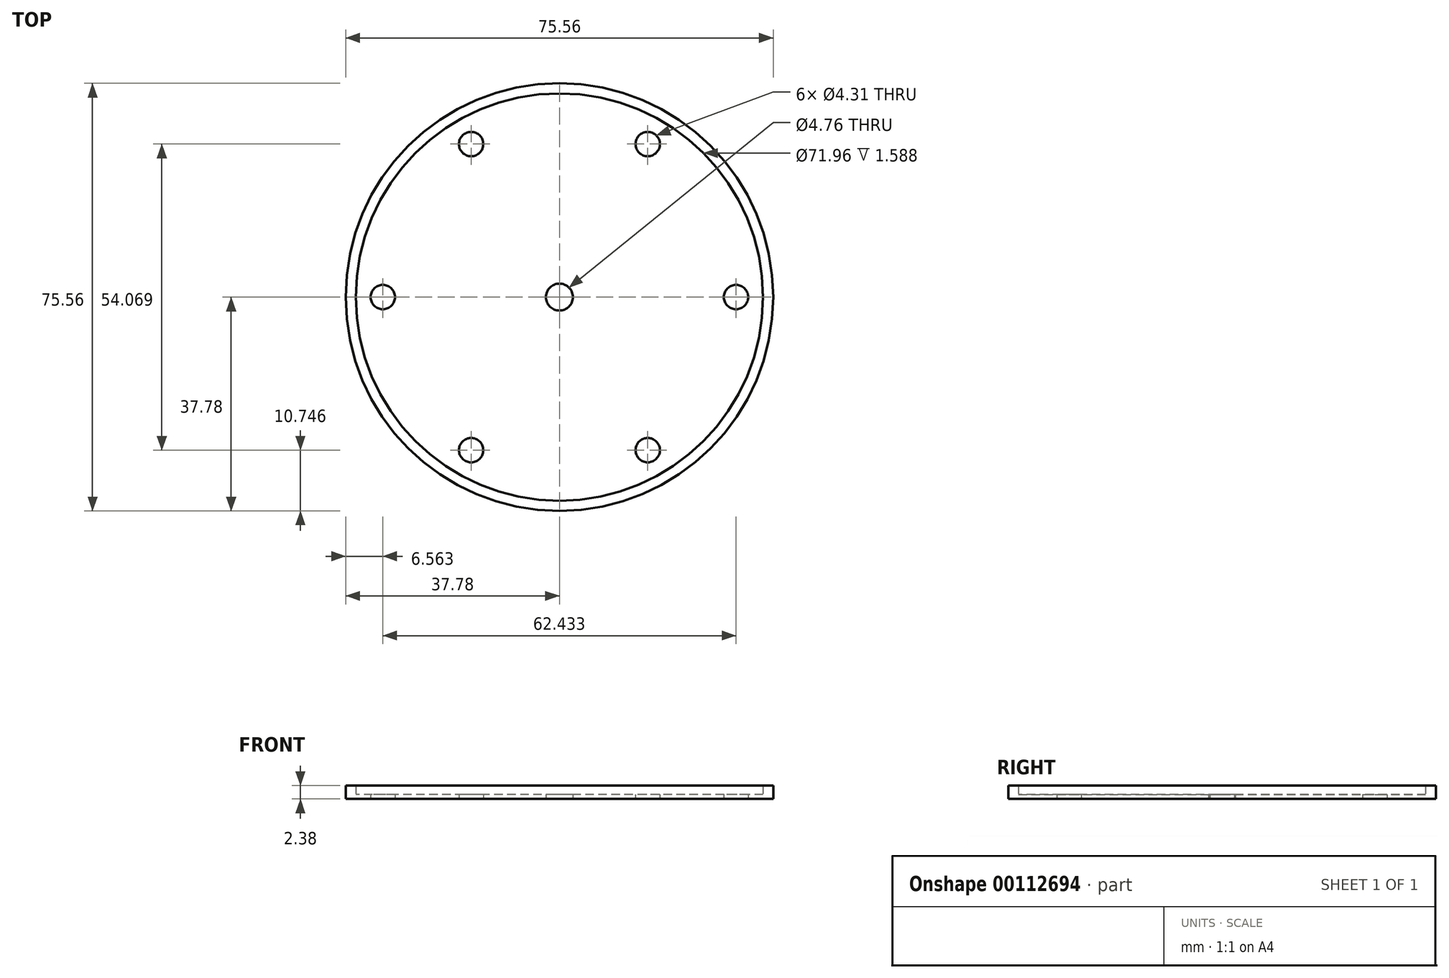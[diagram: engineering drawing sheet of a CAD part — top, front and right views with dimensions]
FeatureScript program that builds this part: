
annotation { "Feature Type Name" : "Feature", "Feature Type Description" : "" }
export const myFeature = defineFeature(function(context is Context, id is Id, definition is map)
    precondition{}
    {
        {
            var Q0;
            Q0=qCreatedBy(makeId("Top.planeOp"),FACE);
            var sketch = newSketch(context, id + "F0", { "sketchPlane" : qUnion([Q0])});
            skCircle(sketch, "E0", {"center": v(0, 0) * mm, "radius": 37.78 * mm});
            skCircle(sketch, "E1", {"center": v(0, 0) * mm, "radius": 35.98 * mm, "construction": true});
            skCircle(sketch, "E2.cCircle", {"center": v(0, 0) * mm, "radius": 27.03 * mm, "construction": true});
            skLineSegment(sketch, "E2.0", {"start": v(-15.6, 27.03) * mm, "end": v(15.6, 27.03) * mm, "construction": true});
            skLineSegment(sketch, "E2.1", {"start": v(15.6, 27.03) * mm, "end": v(31.22, 0) * mm, "construction": true});
            skLineSegment(sketch, "E2.2", {"start": v(31.22, 0) * mm, "end": v(15.6, -27.03) * mm, "construction": true});
            skLineSegment(sketch, "E2.3", {"start": v(15.6, -27.03) * mm, "end": v(-15.6, -27.03) * mm, "construction": true});
            skLineSegment(sketch, "E2.4", {"start": v(-15.6, -27.03) * mm, "end": v(-31.22, 0) * mm, "construction": true});
            skLineSegment(sketch, "E2.5", {"start": v(-31.22, 0) * mm, "end": v(-15.6, 27.03) * mm, "construction": true});
            skPoint(sketch, "E2.0.midPoint", {"position": v(0, 27.03) * mm});
            skCircle(sketch, "E3", {"center": v(-15.6, 27.03) * mm, "radius": 4.76 * mm, "construction": true});
            skCircle(sketch, "E4", {"center": v(-15.6, 27.03) * mm, "radius": 2.15 * mm});
            skCircle(sketch, "E5", {"center": v(-31.22, 0) * mm, "radius": 2.15 * mm});
            skCircle(sketch, "E6", {"center": v(-15.6, -27.03) * mm, "radius": 2.15 * mm});
            skCircle(sketch, "E7", {"center": v(15.6, -27.03) * mm, "radius": 2.15 * mm});
            skCircle(sketch, "E8", {"center": v(31.22, 0) * mm, "radius": 2.15 * mm});
            skCircle(sketch, "E9", {"center": v(15.6, 27.03) * mm, "radius": 2.15 * mm});
            skCircle(sketch, "E10", {"center": v(0, 0) * mm, "radius": 2.38 * mm});
            skSolve(sketch);
        }
        {
            var Q0;
            Q0 = qSketchRegion(id + "F0", true);
            extrude(context, id + "F1", {"entities" : qUnion([Q0]), "depth" : 0.8 * mm});
        }
        {
            var Q0;
            Q0=makeQuery(id+"F1.opExtrude","CAP_FACE",FACE,{"disambiguationData":[OSD([sQuery(id+"F0.wireOp",EDGE,"E0")])],"isStart":false});
            var sketch = newSketch(context, id + "F2", { "sketchPlane" : qUnion([Q0])});
            skCircle(sketch, "E11", {"center": v(0, 0) * mm, "radius": 35.98 * mm});
            skCircle(sketch, "E12", {"center": v(0, 0) * mm, "radius": 37.78 * mm});
            skSolve(sketch);
        }
        {
            var Q0;
            Q0 = qSketchRegion(id + "F2", true);
            extrude(context, id + "F3", {"entities" : qUnion([Q0]), "operationType" : NewBodyOperationType.ADD, "depth" : 1.59 * mm});
        }
    });
